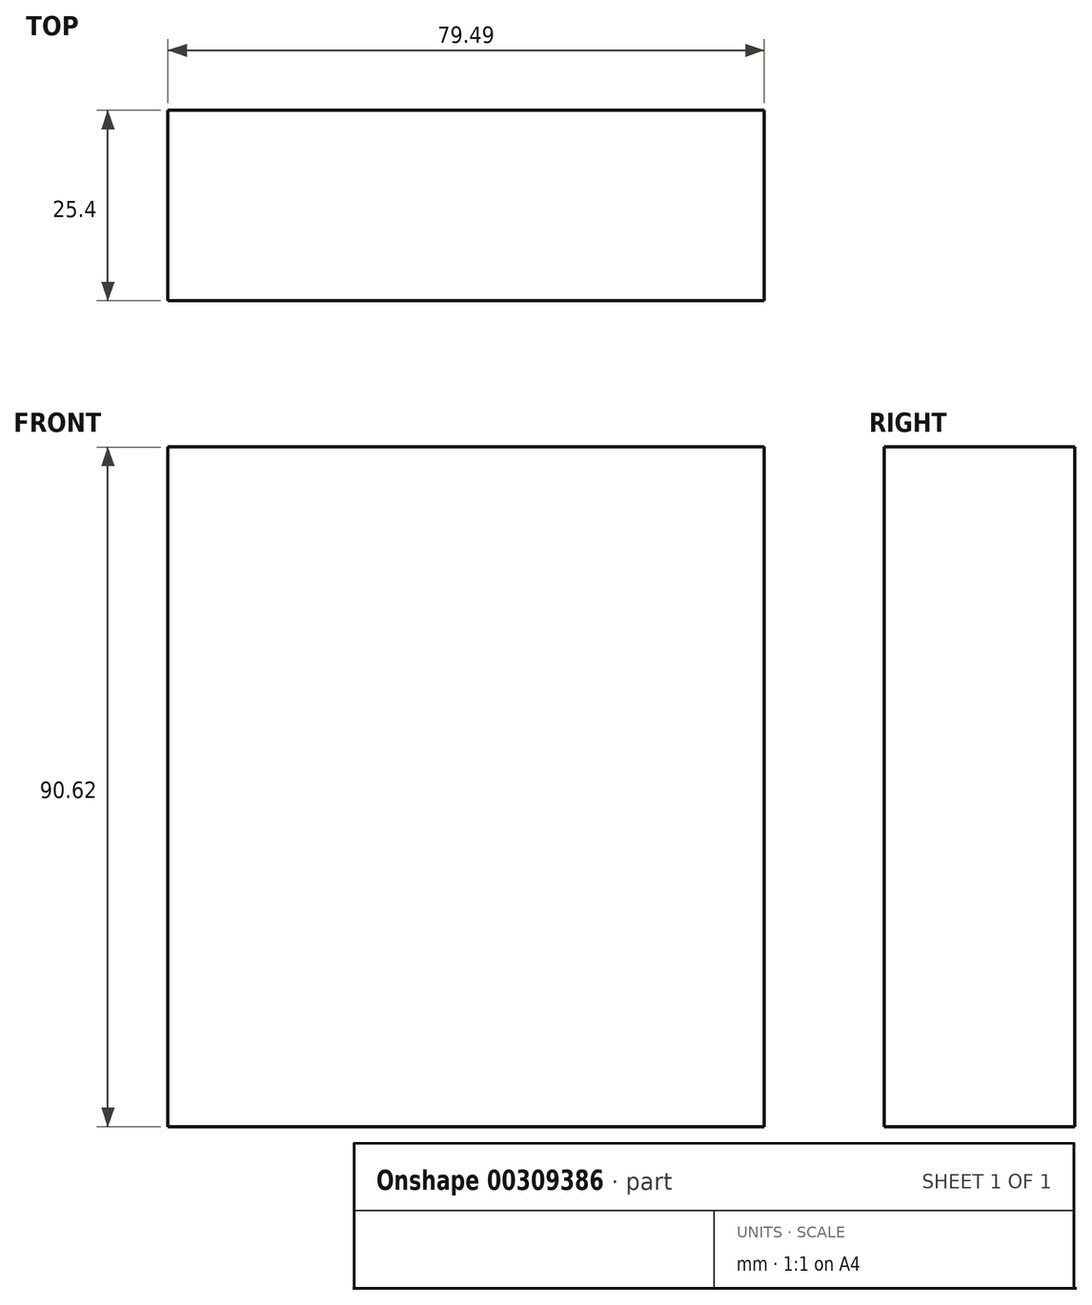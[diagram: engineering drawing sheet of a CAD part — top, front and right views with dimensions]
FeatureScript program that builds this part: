
annotation { "Feature Type Name" : "Feature", "Feature Type Description" : "" }
export const myFeature = defineFeature(function(context is Context, id is Id, definition is map)
    precondition{}
    {
        {
            var Q0;
            Q0=qCreatedBy(makeId("Front.planeOp"),FACE);
            var sketch = newSketch(context, id + "F0", { "sketchPlane" : qUnion([Q0])});
            skLineSegment(sketch, "E0.bottom", {"start": v(0, 0) * mm, "end": v(79.49, 0) * mm});
            skLineSegment(sketch, "E0.top", {"start": v(0, 90.62) * mm, "end": v(79.49, 90.62) * mm});
            skLineSegment(sketch, "E0.left", {"start": v(0, 0) * mm, "end": v(0, 90.62) * mm});
            skLineSegment(sketch, "E0.right", {"start": v(79.49, 0) * mm, "end": v(79.49, 90.62) * mm});
            skSolve(sketch);
        }
        {
            var Q0;
            Q0 = qSketchRegion(id + "F0", true);
            extrude(context, id + "F1", {"entities" : qUnion([Q0]), "depth" : 25.4 * mm});
        }
    });
